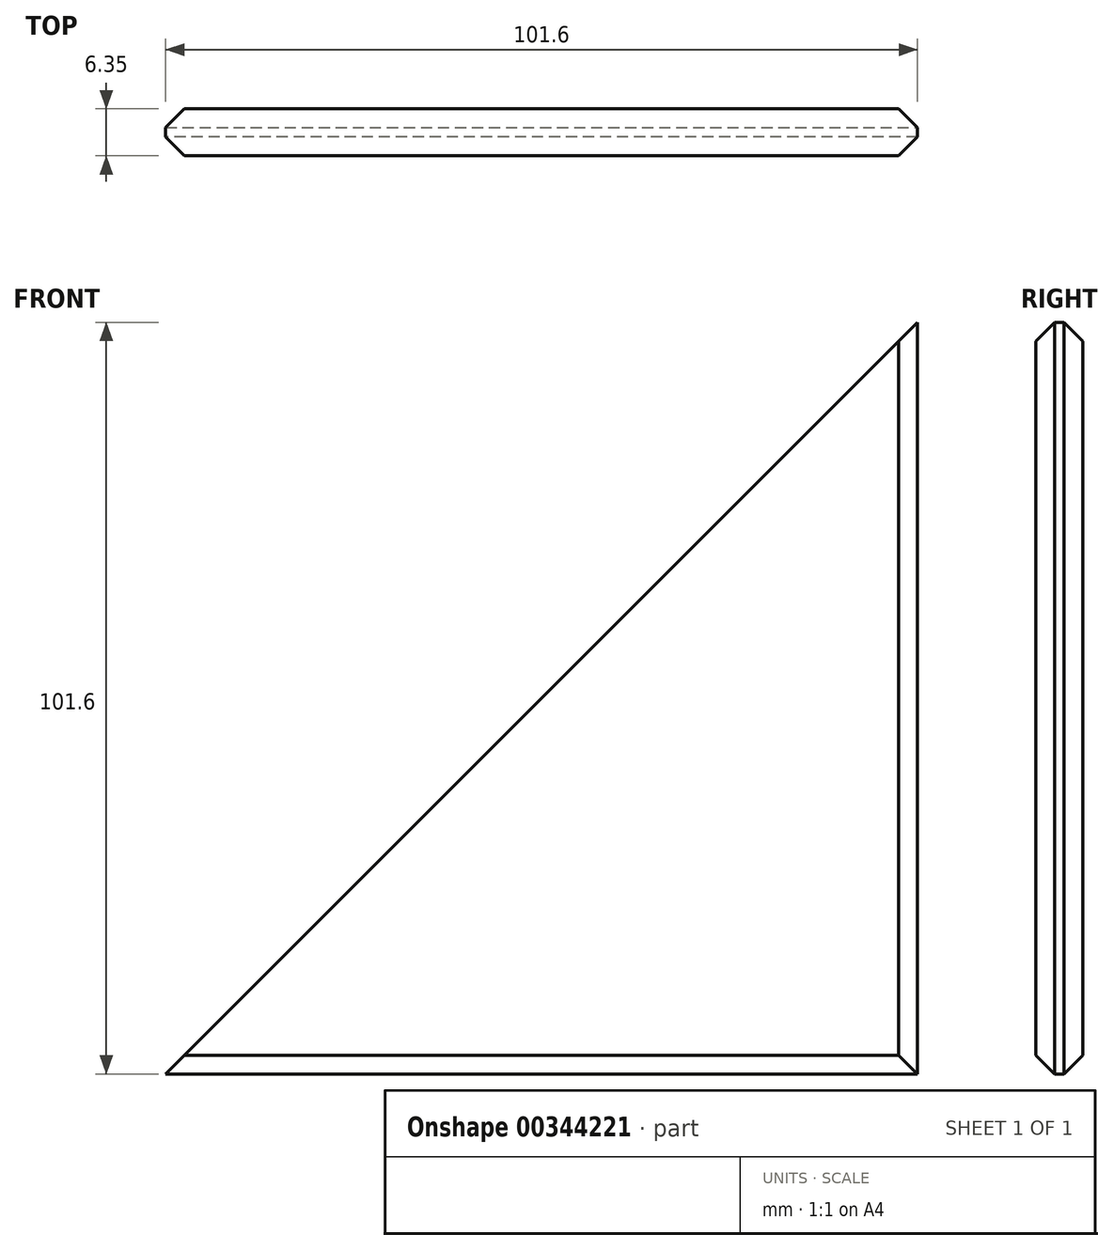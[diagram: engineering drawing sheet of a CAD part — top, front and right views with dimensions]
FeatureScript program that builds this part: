
annotation { "Feature Type Name" : "Feature", "Feature Type Description" : "" }
export const myFeature = defineFeature(function(context is Context, id is Id, definition is map)
    precondition{}
    {
        {
            var Q0;
            Q0=qCreatedBy(makeId("Front.planeOp"),FACE);
            var sketch = newSketch(context, id + "F0", { "sketchPlane" : qUnion([Q0])});
            skLineSegment(sketch, "E0", {"start": v(0, 0) * mm, "end": v(101.6, 101.6) * mm});
            skLineSegment(sketch, "E1", {"start": v(101.6, 101.6) * mm, "end": v(101.6, 0) * mm});
            skLineSegment(sketch, "E2", {"start": v(101.6, 0) * mm, "end": v(0, 0) * mm});
            skSolve(sketch);
        }
        {
            var Q0;
            Q0=makeQuery(id+"F0.imprint","IMPRINT",FACE,{"disambiguationData":[TD([[makeQuery(id+"F0.imprint","IMPRINT",EDGE,{"derivedFrom":sQuery(id+"F0.wireOp",EDGE,"E0")}),-1.0]])]});
            extrude(context, id + "F1", {"entities" : qUnion([Q0]), "depth" : 6.35 * mm});
        }
        {
            var Q0;
            Q0=makeQuery(id+"F1.opExtrude","CAP_EDGE",EDGE,{"disambiguationData":[OSD([sQuery(id+"F0.wireOp",EDGE,"E1")])],"isStart":false});
            var Q1;
            Q1=makeQuery(id+"F1.opExtrude","CAP_EDGE",EDGE,{"disambiguationData":[OSD([sQuery(id+"F0.wireOp",EDGE,"E2")])],"isStart":false});
            chamfer(context, id + "F2", {"entities" : qUnion([Q0, Q1]), "width" : 2.54 * mm, "tangentPropagation" : true});
        }
        {
            var Q0;
            Q0=makeQuery(id+"F1.opExtrude","CAP_EDGE",EDGE,{"disambiguationData":[OSD([sQuery(id+"F0.wireOp",EDGE,"E1")])],"isStart":true});
            var Q1;
            Q1=makeQuery(id+"F1.opExtrude","CAP_EDGE",EDGE,{"disambiguationData":[OSD([sQuery(id+"F0.wireOp",EDGE,"E2")])],"isStart":true});
            chamfer(context, id + "F3", {"entities" : qUnion([Q0, Q1]), "width" : 2.54 * mm, "tangentPropagation" : true});
        }
    });
